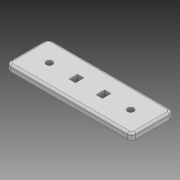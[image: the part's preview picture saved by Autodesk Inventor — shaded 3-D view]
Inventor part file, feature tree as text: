
AUTODESK INVENTOR PART (.ipt)
format: ipt  version: 2018 (Build 220112000, 112)  size: 123,904 bytes
history: native  units: mm
features: fillet x2, other x1, extrude x1, sketch x1
ambient origin geometry x8: Origin, YZ Plane, XZ Plane, XY Plane, X Axis, Y Axis, Z Axis, Center Point
bodies: Body1 (feature_tree)
feature tree (5):
  other  "Sólido1"
  extrude  "Extrusión1"  Depth=20.0mm
  fillet  "Empalme1"  Radius=19.5mm
  fillet  "Empalme2"  Radius=19.5mm
  sketch  "Boceto1"  dims[d0=60.0mm d1=20.0mm d2=19.5mm d3=19.5mm d4=10.0mm d5=3.0mm d6=3.0mm d7=5.0mm d8=3.0mm d9=2.0mm d10=2.0mm d11=5.0mm d12=3.0mm d13=3.0mm d14=0.0mm d15=2.0mm d16=1.0mm]
